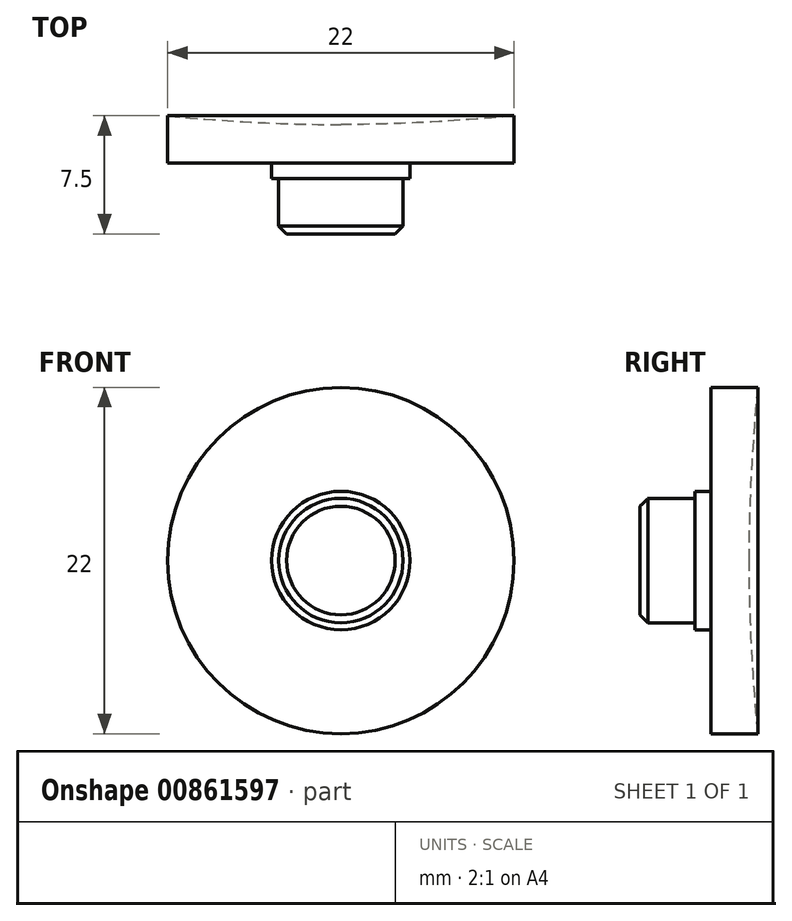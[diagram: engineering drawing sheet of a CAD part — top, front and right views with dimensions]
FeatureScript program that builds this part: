
annotation { "Feature Type Name" : "Feature", "Feature Type Description" : "" }
export const myFeature = defineFeature(function(context is Context, id is Id, definition is map)
    precondition{}
    {
        {
            var Q0;
            Q0=qCreatedBy(makeId("Top.planeOp"),FACE);
            var sketch = newSketch(context, id + "F0", { "sketchPlane" : qUnion([Q0])});
            skLineSegment(sketch, "E0", {"start": v(-11, 7.5) * mm, "end": v(-11, 4.5) * mm});
            skLineSegment(sketch, "E1", {"start": v(-11, 4.5) * mm, "end": v(-4.4, 4.5) * mm});
            skLineSegment(sketch, "E2", {"start": v(-4.4, 4.5) * mm, "end": v(-4.4, 3.5) * mm});
            skLineSegment(sketch, "E3", {"start": v(-4.4, 3.5) * mm, "end": v(-3.95, 3.5) * mm});
            skLineSegment(sketch, "E4", {"start": v(-3.95, 3.5) * mm, "end": v(-3.95, 0) * mm});
            skLineSegment(sketch, "E5", {"start": v(-3.95, 0) * mm, "end": v(0, 0) * mm});
            skLineSegment(sketch, "E6", {"start": v(0, 0) * mm, "end": v(0, 7.5) * mm});
            skArc(sketch, "E7", {"start": v(-11, 7.5) * mm, "mid": v(-5.5, 7.1) * mm, "end": v(0, 6.94) * mm});
            skSolve(sketch);
        }
        {
            var Q0;
            Q0=makeQuery(id+"F0.imprint","IMPRINT",FACE,{"disambiguationData":[TD([[makeQuery(id+"F0.imprint","IMPRINT",EDGE,{"derivedFrom":sQuery(id+"F0.wireOp",EDGE,"E0")}),1.0]])]});
            var Q1;
            Q1=sQuery(id+"F0.wireOp",EDGE,"E6");
            revolve(context, id + "F1", {"surfaceOperationType" : NewSurfaceOperationType.NEW, "entities" : qUnion([Q0]), "axis" : qUnion([Q1]), "revolveType" : RevolveType.FULL});
        }
        {
            var Q0;
            Q0=makeQuery(id+"F1.opRevolve","SWEPT_FACE",FACE,{"disambiguationData":[OSD([sQuery(id+"F0.wireOp",EDGE,"E5")])]});
            chamfer(context, id + "F2", {"entities" : qUnion([Q0]), "width" : .5 * mm, "tangentPropagation" : true});
        }
    });
